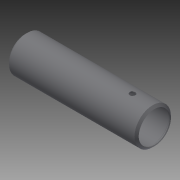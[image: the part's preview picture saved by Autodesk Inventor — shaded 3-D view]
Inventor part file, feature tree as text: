
AUTODESK INVENTOR PART (.ipt)
format: ipt  version: 2014 (Build 180170000, 170)  size: 133,632 bytes
history: native  units: in
note: dims shown in document units (in); Inventor stores cm internally (conversion verified against a paired STEP export)
features: other x56, revolve x2, sketch x2
ambient origin geometry x8: Origin, YZ Plane, XZ Plane, XY Plane, X Axis, Y Axis, Z Axis, Center Point
bodies: Solid1 (feature_tree)
feature tree (60):
  revolve  "Revolution1"  Angle=360.0deg
  revolve  "Revolution2"  [1 undecoded]
  other  "o1_XY"
  other  "o1_YZ"
  other  "o1_ZX"
  other  "o1_X"
  other  "o1_Y"
  other  "o1_Z"
  other  "o1_Center"
  other  "o2_XY"
  other  "o2_YZ"
  other  "o2_ZX"
  other  "o2_X"
  other  "o2_Y"
  other  "o2_Z"
  other  "o2_Center"
  other  "t1_XY"
  other  "t1_YZ"
  other  "t1_ZX"
  other  "t1_X"
  other  "t1_Y"
  other  "t1_Z"
  other  "t1_Center"
  other  "t2_XY"
  other  "t2_YZ"
  other  "t2_ZX"
  other  "t2_X"
  other  "t2_Y"
  other  "t2_Z"
  other  "t2_Center"
  other  "t3_XY"
  other  "t3_YZ"
  other  "t3_ZX"
  other  "t3_X"
  other  "t3_Y"
  other  "t3_Z"
  other  "t3_Center"
  other  "t4_XY"
  other  "t4_YZ"
  other  "t4_ZX"
  other  "t4_X"
  other  "t4_Y"
  other  "t4_Z"
  other  "t4_Center"
  other  "tube1_XY"
  other  "tube1_YZ"
  other  "tube1_ZX"
  other  "tube1_X"
  other  "tube1_Y"
  other  "tube1_Z"
  other  "tube1_Center"
  other  "tube2_XY"
  other  "tube2_YZ"
  other  "tube2_ZX"
  other  "tube2_X"
  other  "tube2_Y"
  other  "tube2_Z"
  other  "tube2_Center"
  sketch  "Sketch_5"
  sketch  "Sketch_1"  dims[d0=360.0deg d1=360.0deg]
note: 1 required parameter value undecoded (feature->parameter linkage not recoverable at this tier; creation-order binding heuristic only, values carry confidence <= 0.55)
